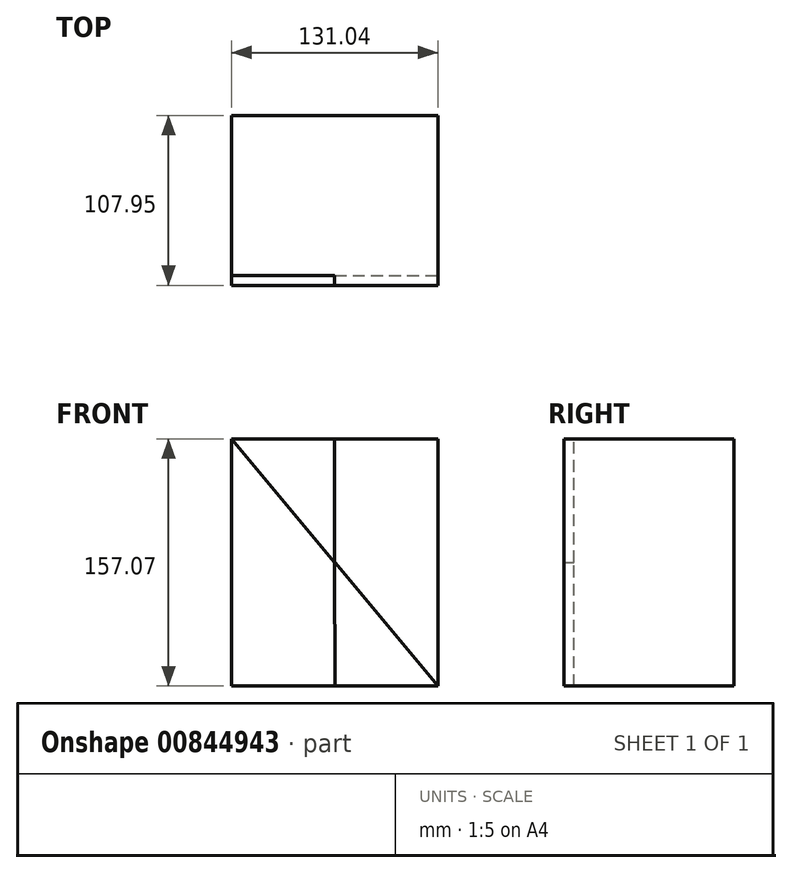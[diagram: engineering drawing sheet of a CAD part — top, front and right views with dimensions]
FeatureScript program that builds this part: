
annotation { "Feature Type Name" : "Feature", "Feature Type Description" : "" }
export const myFeature = defineFeature(function(context is Context, id is Id, definition is map)
    precondition{}
    {
        {
            var Q0;
            Q0=qCreatedBy(makeId("Front.planeOp"),FACE);
            var sketch = newSketch(context, id + "F0", { "sketchPlane" : qUnion([Q0])});
            skLineSegment(sketch, "E0.bottom", {"start": v(-65.43, 78.34) * mm, "end": v(65.61, 78.34) * mm});
            skLineSegment(sketch, "E0.top", {"start": v(-65.43, -78.73) * mm, "end": v(65.61, -78.73) * mm});
            skLineSegment(sketch, "E0.left", {"start": v(-65.43, 78.34) * mm, "end": v(-65.43, -78.73) * mm});
            skLineSegment(sketch, "E0.right", {"start": v(65.61, 78.34) * mm, "end": v(65.61, -78.73) * mm});
            skPoint(sketch, "E0.middle", {"position": v(0.1, -0.2) * mm});
            skSolve(sketch);
        }
        {
            var Q0;
            Q0=makeQuery(id+"F0.imprint","IMPRINT",FACE,{"disambiguationData":[TD([[makeQuery(id+"F0.imprint","IMPRINT",EDGE,{"derivedFrom":sQuery(id+"F0.wireOp",EDGE,"E0.bottom")}),-1.0]])]});
            extrude(context, id + "F1", {"entities" : qUnion([Q0]), "endBound" : BoundingType.SYMMETRIC, "depth" : 76.2 * mm, "offsetDistance" : 25.4 * mm});
        }
        {
            var Q0;
            Q0=makeQuery(id+"F1.opExtrude","CAP_FACE",FACE,{"disambiguationData":[OSD([sQuery(id+"F0.wireOp",EDGE,"E0.bottom"),sQuery(id+"F0.wireOp",EDGE,"E0.top"),sQuery(id+"F0.wireOp",EDGE,"E0.left"),sQuery(id+"F0.wireOp",EDGE,"E0.right")])],"isStart":false});
            var sketch = newSketch(context, id + "F2", { "sketchPlane" : qUnion([Q0])});
            skLineSegment(sketch, "E1", {"start": v(65.61, 78.34) * mm, "end": v(-65.43, -78.73) * mm});
            skLineSegment(sketch, "E2", {"start": v(-65.43, -78.73) * mm, "end": v(65.61, -78.73) * mm});
            skLineSegment(sketch, "E3", {"start": v(65.61, -78.73) * mm, "end": v(-65.43, 78.34) * mm});
            skLineSegment(sketch, "E4", {"start": v(65.61, -0.2) * mm, "end": v(-65.43, 0) * mm});
            skLineSegment(sketch, "E5", {"start": v(0.1, -78.73) * mm, "end": v(0, 78.34) * mm});
            skPoint(sketch, "E5.endSnap0", {"position": v(0.1, 78.34) * mm});
            skSolve(sketch);
        }
        {
            var Q0;
            {var subQ0=sQuery(id+"F2.wireOp",EDGE,"E3");var subQ1=sQuery(id+"F2.wireOp",EDGE,"E1");var subQ2=makeQuery(id+"F2.imprint","INTERSECT",VERTEX,{"derivedFrom":[subQ1,subQ0]});Q0=makeQuery(id+"F2.imprint","IMPRINT",FACE,{"disambiguationData":[TD([[makeQuery(id+"F2.imprint","IMPRINT",EDGE,{"disambiguationData":[TD([[subQ2,-1.0]])],"derivedFrom":subQ1}),1.0]])]});}
            var Q1;
            {var subQ0=sQuery(id+"F2.wireOp",EDGE,"E3");var subQ3=sQuery(id+"F2.wireOp",EDGE,"E4");var subQ4=makeQuery(id+"F2.imprint","INTERSECT",VERTEX,{"derivedFrom":[subQ0,subQ3]});Q1=makeQuery(id+"F2.imprint","IMPRINT",FACE,{"disambiguationData":[TD([[makeQuery(id+"F2.imprint","IMPRINT",EDGE,{"disambiguationData":[TD([[subQ4,1.0]])],"derivedFrom":subQ3}),-1.0]])]});}
            extrude(context, id + "F3", {"entities" : qUnion([Q0, Q1]), "operationType" : NewBodyOperationType.ADD, "depth" : 25.4 * mm, "offsetDistance" : 25.4 * mm});
        }
        {
            var Q0;
            Q0=makeQuery(id+"F1.opExtrude","CAP_FACE",FACE,{"disambiguationData":[OSD([sQuery(id+"F0.wireOp",EDGE,"E0.bottom"),sQuery(id+"F0.wireOp",EDGE,"E0.top"),sQuery(id+"F0.wireOp",EDGE,"E0.left"),sQuery(id+"F0.wireOp",EDGE,"E0.right")])],"isStart":false});
            extrude(context, id + "F4", {"entities" : qUnion([Q0]), "operationType" : NewBodyOperationType.ADD, "depth" : 31.75 * mm, "offsetDistance" : 25.4 * mm});
        }
        {
            var Q0;
            Q0=makeQuery(id+"F1.opExtrude","CAP_FACE",FACE,{"disambiguationData":[OSD([sQuery(id+"F0.wireOp",EDGE,"E0.bottom"),sQuery(id+"F0.wireOp",EDGE,"E0.top"),sQuery(id+"F0.wireOp",EDGE,"E0.left"),sQuery(id+"F0.wireOp",EDGE,"E0.right")])],"isStart":true});
            extrude(context, id + "F5", {"entities" : qUnion([Q0]), "operationType" : NewBodyOperationType.ADD, "depth" : -25.4 * mm, "offsetDistance" : 25.4 * mm});
        }
        {
            var Q0;
            Q0=makeQuery(id+"F1.opExtrude","CAP_FACE",FACE,{"disambiguationData":[OSD([sQuery(id+"F0.wireOp",EDGE,"E0.bottom"),sQuery(id+"F0.wireOp",EDGE,"E0.top"),sQuery(id+"F0.wireOp",EDGE,"E0.left"),sQuery(id+"F0.wireOp",EDGE,"E0.right")])],"isStart":true});
            extrude(context, id + "F6", {"entities" : qUnion([Q0]), "operationType" : NewBodyOperationType.ADD, "depth" : -25.4 * mm, "offsetDistance" : 25.4 * mm});
        }
    });
